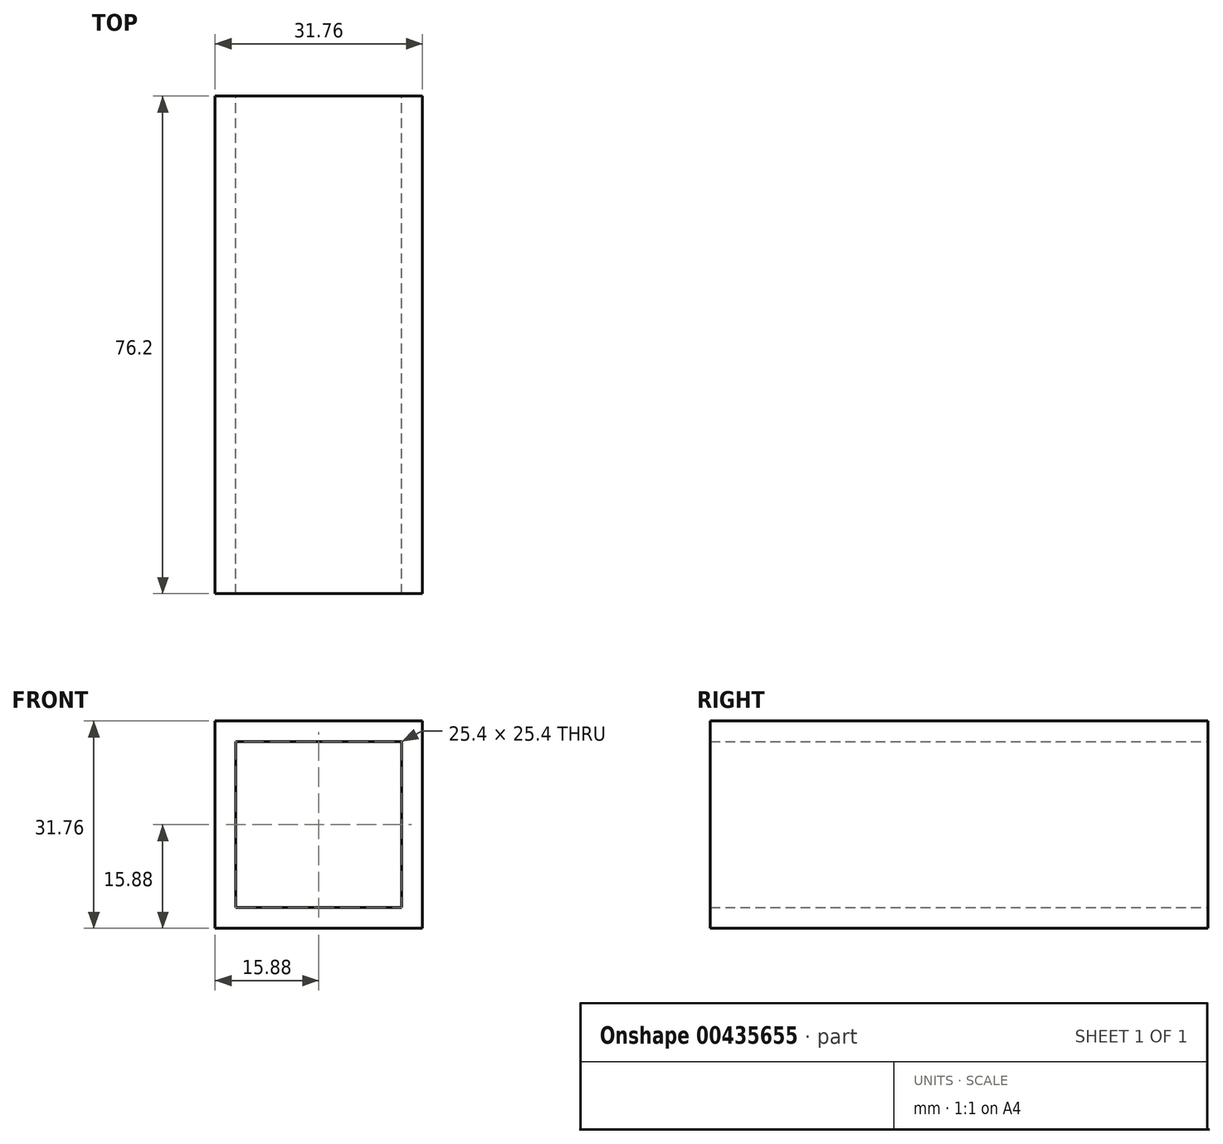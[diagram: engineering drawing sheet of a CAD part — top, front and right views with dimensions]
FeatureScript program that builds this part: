
annotation { "Feature Type Name" : "Feature", "Feature Type Description" : "" }
export const myFeature = defineFeature(function(context is Context, id is Id, definition is map)
    precondition{}
    {
        {
            var Q0;
            Q0=qCreatedBy(makeId("Front.planeOp"),FACE);
            var sketch = newSketch(context, id + "F0", { "sketchPlane" : qUnion([Q0])});
            skLineSegment(sketch, "E0.bottom", {"start": v(12.7, -12.7) * mm, "end": v(-12.7, -12.7) * mm});
            skLineSegment(sketch, "E0.top", {"start": v(12.7, 12.7) * mm, "end": v(-12.7, 12.7) * mm});
            skLineSegment(sketch, "E0.left", {"start": v(12.7, -12.7) * mm, "end": v(12.7, 12.7) * mm});
            skLineSegment(sketch, "E0.right", {"start": v(-12.7, -12.7) * mm, "end": v(-12.7, 12.7) * mm});
            skPoint(sketch, "E0.middle", {"position": v(0, 0) * mm});
            skLineSegment(sketch, "E1.0", {"start": v(15.88, 15.88) * mm, "end": v(-15.87, 15.87) * mm});
            skLineSegment(sketch, "E1.1", {"start": v(15.88, -15.87) * mm, "end": v(15.88, 15.88) * mm});
            skLineSegment(sketch, "E1.2", {"start": v(15.88, -15.87) * mm, "end": v(-15.87, -15.88) * mm});
            skLineSegment(sketch, "E1.3", {"start": v(-15.87, -15.88) * mm, "end": v(-15.87, 15.87) * mm});
            skSolve(sketch);
        }
        {
            var Q0;
            Q0 = qSketchRegion(id + "F0", true);
            extrude(context, id + "F1", {"entities" : qUnion([Q0]), "depth" : 76.2 * mm});
        }
    });
